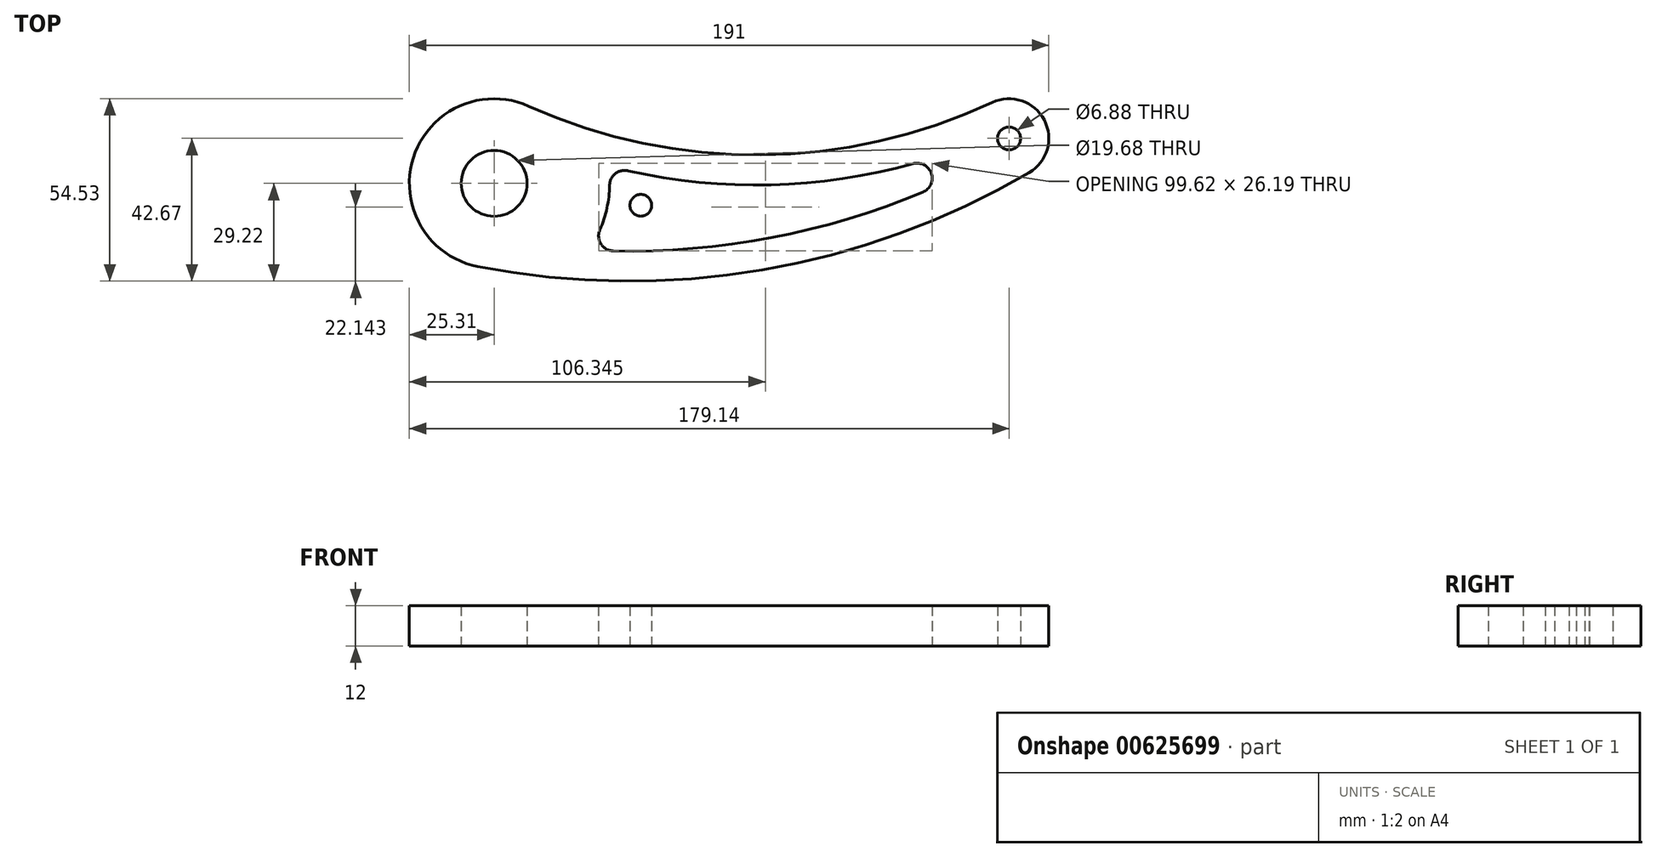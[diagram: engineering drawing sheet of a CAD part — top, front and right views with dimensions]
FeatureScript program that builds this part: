
annotation { "Feature Type Name" : "Feature", "Feature Type Description" : "" }
export const myFeature = defineFeature(function(context is Context, id is Id, definition is map)
    precondition{}
    {
        {
            var Q0;
            Q0=qCreatedBy(makeId("Top.planeOp"),FACE);
            var sketch = newSketch(context, id + "F0", { "sketchPlane" : qUnion([Q0])});
            skLineSegment(sketch, "E0", {"start": v(-153.83, 0) * mm, "end": v(0, 0) * mm});
            skCircle(sketch, "E1", {"center": v(0, -11.86) * mm, "radius": 3.44 * mm});
            skCircle(sketch, "E2", {"center": v(-153.83, -25.3) * mm, "radius": 9.84 * mm});
            skArc(sketch, "E3", {"start": v(-143.46, -2.22) * mm, "mid": v(-177.95, -17.65) * mm, "end": v(-158.68, -50.15) * mm});
            skArc(sketch, "E4", {"start": v(-143.46, -2.22) * mm, "mid": v(-74.13, -16.79) * mm, "end": v(-5.03, -1.12) * mm});
            skArc(sketch, "E5", {"start": v(-158.68, -50.15) * mm, "mid": v(-73.78, -51.18) * mm, "end": v(6, -22.09) * mm});
            skArc(sketch, "E6", {"start": v(-113.85, -21.53) * mm, "mid": v(-71.14, -25.74) * mm, "end": v(-28.68, -19.43) * mm});
            skArc(sketch, "E7.trimOffspring", {"start": v(-122.24, -39.17) * mm, "mid": v(-120.12, -32.66) * mm, "end": v(-119.33, -25.85) * mm});
            skPoint(sketch, "E8.orphan", {"position": v(-185.73, 0) * mm});
            skArc(sketch, "E9.trimOffspring", {"start": v(-118.21, -45.48) * mm, "mid": v(-71.06, -41.55) * mm, "end": v(-25.74, -27.92) * mm});
            skArc(sketch, "E10.trimOffspring", {"start": v(6, -22.09) * mm, "mid": v(10.5, -6.34) * mm, "end": v(-5.03, -1.12) * mm});
            skArc(sketch, "E11", {"start": v(-25.74, -27.92) * mm, "mid": v(-23.23, -22.3) * mm, "end": v(-28.68, -19.43) * mm});
            skPoint(sketch, "E12.visualSharp", {"position": v(-119.73, -20.1) * mm});
            skArc(sketch, "E12.filletArc", {"start": v(-113.85, -21.53) * mm, "mid": v(-117.62, -22.38) * mm, "end": v(-119.33, -25.85) * mm});
            skPoint(sketch, "E13.visualSharp", {"position": v(-125.64, -45.2) * mm});
            skArc(sketch, "E13.filletArc", {"start": v(-122.24, -39.17) * mm, "mid": v(-121.91, -43.4) * mm, "end": v(-118.21, -45.48) * mm});
            skLineSegment(sketch, "E14", {"start": v(0, -11.86) * mm, "end": v(13.02, -11.86) * mm});
            skLineSegment(sketch, "E15", {"start": v(-153.83, -25.3) * mm, "end": v(-198.86, -25.3) * mm});
            skCircle(sketch, "E16", {"center": v(-110, -31.86) * mm, "radius": 3.25 * mm});
            skCircle(sketch, "E17", {"center": v(-50, -31.86) * mm, "radius": 3.25 * mm});
            skSolve(sketch);
        }
        {
            var Q0;
            Q0=makeQuery(id+"F0.imprint","IMPRINT",FACE,{"disambiguationData":[TD([[makeQuery(id+"F0.imprint","IMPRINT",EDGE,{"derivedFrom":sQuery(id+"F0.wireOp",EDGE,"E1")}),-1.0]])]});
            var Q1;
            Q1=makeQuery(id+"F0.imprint","IMPRINT",FACE,{"disambiguationData":[TD([[makeQuery(id+"F0.imprint","IMPRINT",EDGE,{"derivedFrom":sQuery(id+"F0.wireOp",EDGE,"E16")}),1.0]])]});
            extrude(context, id + "F1", {"entities" : qUnion([Q0, Q1]), "depth" : 12 * mm, "offsetDistance" : 25 * mm});
        }
    });
